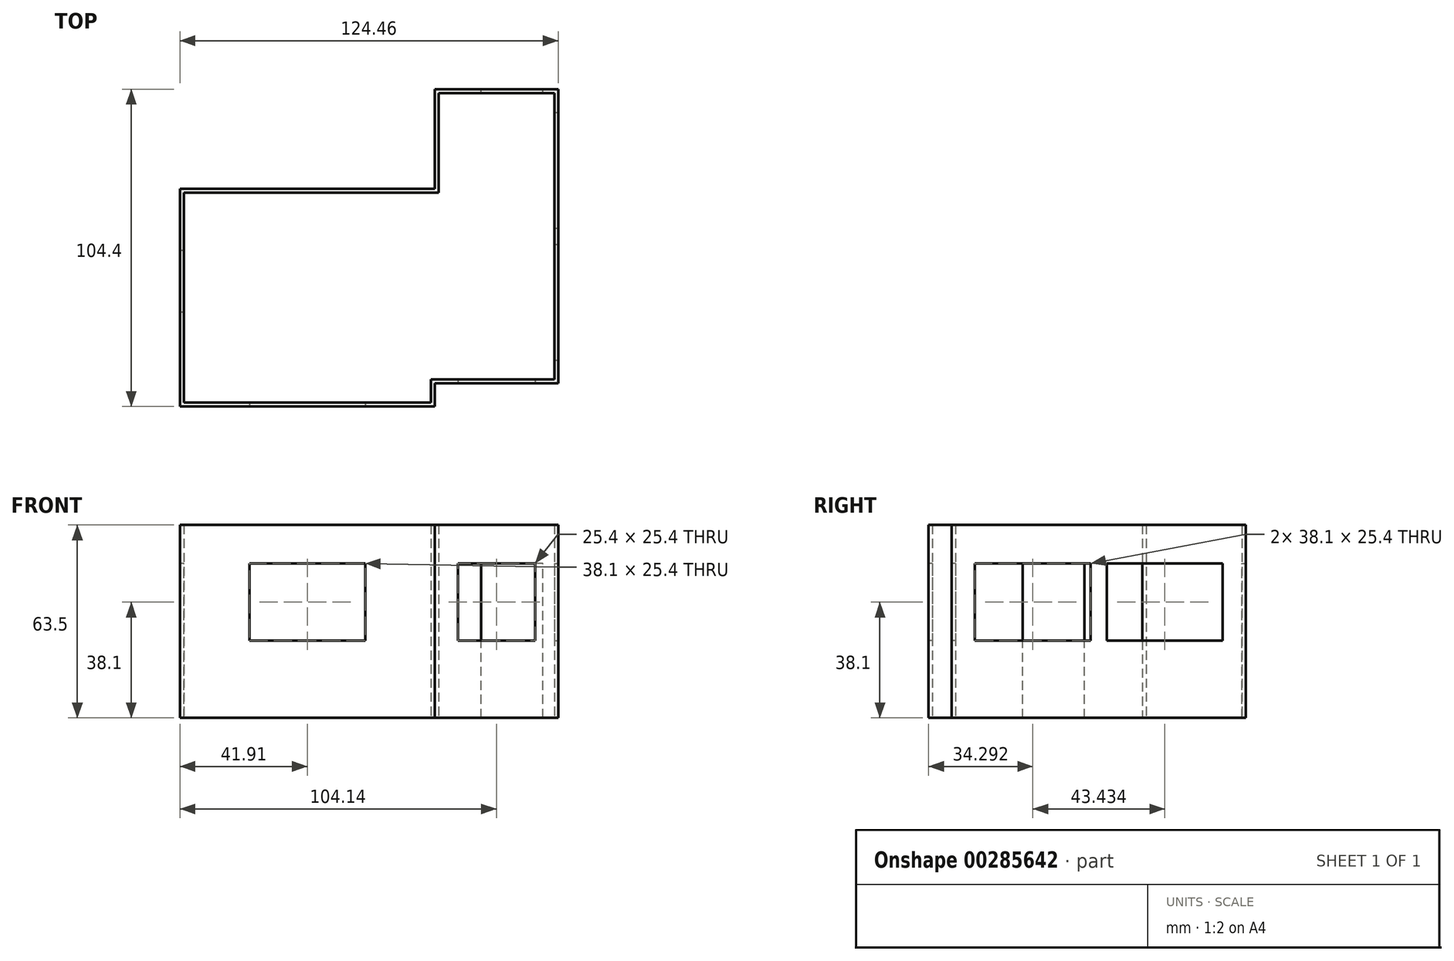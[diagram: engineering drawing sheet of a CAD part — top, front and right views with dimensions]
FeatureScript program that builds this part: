
annotation { "Feature Type Name" : "Feature", "Feature Type Description" : "" }
export const myFeature = defineFeature(function(context is Context, id is Id, definition is map)
    precondition{}
    {
        {
            var Q0;
            Q0=qCreatedBy(makeId("Top.planeOp"),FACE);
            var sketch = newSketch(context, id + "F0", { "sketchPlane" : qUnion([Q0])});
            skLineSegment(sketch, "E0.bottom", {"start": v(0, 0) * mm, "end": v(-83.82, 0) * mm});
            skLineSegment(sketch, "E0.top", {"start": v(0, -71.63) * mm, "end": v(-83.82, -71.63) * mm});
            skLineSegment(sketch, "E0.left", {"start": v(0, -64) * mm, "end": v(0, -71.63) * mm});
            skLineSegment(sketch, "E0.right", {"start": v(-83.82, 0) * mm, "end": v(-83.82, -71.63) * mm});
            skLineSegment(sketch, "E1.bottom", {"start": v(0, -64) * mm, "end": v(40.64, -64) * mm});
            skLineSegment(sketch, "E1.top", {"start": v(0, 32.77) * mm, "end": v(40.64, 32.77) * mm});
            skLineSegment(sketch, "E1.right", {"start": v(40.64, -64) * mm, "end": v(40.64, 32.77) * mm});
            skLineSegment(sketch, "E2", {"start": v(0, 32.77) * mm, "end": v(0, 0) * mm});
            skLineSegment(sketch, "E3.0", {"start": v(1.27, 31.5) * mm, "end": v(1.27, -1.27) * mm});
            skLineSegment(sketch, "E3.1", {"start": v(1.27, 31.5) * mm, "end": v(39.37, 31.5) * mm});
            skLineSegment(sketch, "E3.2", {"start": v(1.27, -1.27) * mm, "end": v(-82.55, -1.27) * mm});
            skLineSegment(sketch, "E3.3", {"start": v(39.37, -62.74) * mm, "end": v(39.37, 31.5) * mm});
            skLineSegment(sketch, "E3.4", {"start": v(-82.55, -1.27) * mm, "end": v(-82.55, -70.36) * mm});
            skLineSegment(sketch, "E3.5", {"start": v(-1.27, -70.36) * mm, "end": v(-82.55, -70.36) * mm});
            skLineSegment(sketch, "E3.6", {"start": v(-1.27, -62.74) * mm, "end": v(-1.27, -70.36) * mm});
            skLineSegment(sketch, "E3.7", {"start": v(-1.27, -62.74) * mm, "end": v(39.37, -62.74) * mm});
            skSolve(sketch);
        }
        {
            var Q0;
            Q0 = qSketchRegion(id + "F0", true);
            extrude(context, id + "F1", {"entities" : qUnion([Q0]), "depth" : 63.5 * mm});
        }
        {
            var Q0;
            Q0=makeQuery(id+"F1.opExtrude","SWEPT_FACE",FACE,{"disambiguationData":[OSD([sQuery(id+"F0.wireOp",EDGE,"E0.top")])]});
            var sketch = newSketch(context, id + "F2", { "sketchPlane" : qUnion([Q0])});
            skLineSegment(sketch, "E4.bottom", {"start": v(-60.96, 50.8) * mm, "end": v(-22.86, 50.8) * mm});
            skLineSegment(sketch, "E4.top", {"start": v(-60.96, 25.4) * mm, "end": v(-22.86, 25.4) * mm});
            skLineSegment(sketch, "E4.left", {"start": v(-60.96, 50.8) * mm, "end": v(-60.96, 25.4) * mm});
            skLineSegment(sketch, "E4.right", {"start": v(-22.86, 50.8) * mm, "end": v(-22.86, 25.4) * mm});
            skSolve(sketch);
        }
        {
            var Q0;
            Q0 = qSketchRegion(id + "F2", true);
            extrude(context, id + "F3", {"entities" : qUnion([Q0]), "operationType" : NewBodyOperationType.REMOVE, "oppositeDirection" : true, "depth" : 1.27 * mm});
        }
        {
            var Q0;
            Q0=makeQuery(id+"F1.opExtrude","SWEPT_FACE",FACE,{"disambiguationData":[OSD([sQuery(id+"F0.wireOp",EDGE,"E1.bottom")])]});
            var sketch = newSketch(context, id + "F4", { "sketchPlane" : qUnion([Q0])});
            skLineSegment(sketch, "E5.bottom", {"start": v(7.62, 50.8) * mm, "end": v(33.02, 50.8) * mm});
            skLineSegment(sketch, "E5.top", {"start": v(7.62, 25.4) * mm, "end": v(33.02, 25.4) * mm});
            skLineSegment(sketch, "E5.left", {"start": v(7.62, 50.8) * mm, "end": v(7.62, 25.4) * mm});
            skLineSegment(sketch, "E5.right", {"start": v(33.02, 50.8) * mm, "end": v(33.02, 25.4) * mm});
            skSolve(sketch);
        }
        {
            var Q0;
            Q0 = qSketchRegion(id + "F4", true);
            extrude(context, id + "F5", {"entities" : qUnion([Q0]), "operationType" : NewBodyOperationType.REMOVE, "oppositeDirection" : true, "depth" : 1.27 * mm});
        }
        {
            var Q0;
            Q0=makeQuery(id+"F1.opExtrude","SWEPT_FACE",FACE,{"disambiguationData":[OSD([sQuery(id+"F0.wireOp",EDGE,"E1.right")])]});
            var sketch = newSketch(context, id + "F6", { "sketchPlane" : qUnion([Q0])});
            skLineSegment(sketch, "E6.bottom", {"start": v(-56.39, 50.8) * mm, "end": v(-18.29, 50.8) * mm});
            skLineSegment(sketch, "E6.top", {"start": v(-56.39, 25.4) * mm, "end": v(-18.29, 25.4) * mm});
            skLineSegment(sketch, "E6.left", {"start": v(-56.39, 50.8) * mm, "end": v(-56.39, 25.4) * mm});
            skLineSegment(sketch, "E6.right", {"start": v(-18.29, 50.8) * mm, "end": v(-18.29, 25.4) * mm});
            skLineSegment(sketch, "E7.bottom", {"start": v(-12.95, 50.8) * mm, "end": v(25.15, 50.8) * mm});
            skLineSegment(sketch, "E7.top", {"start": v(-12.95, 25.4) * mm, "end": v(25.15, 25.4) * mm});
            skLineSegment(sketch, "E7.left", {"start": v(-12.95, 50.8) * mm, "end": v(-12.95, 25.4) * mm});
            skLineSegment(sketch, "E7.right", {"start": v(25.15, 50.8) * mm, "end": v(25.15, 25.4) * mm});
            skSolve(sketch);
        }
        {
            var Q0;
            Q0 = qSketchRegion(id + "F6", true);
            extrude(context, id + "F7", {"entities" : qUnion([Q0]), "operationType" : NewBodyOperationType.REMOVE, "oppositeDirection" : true, "depth" : 1.27 * mm});
        }
        {
            var Q0;
            Q0=makeQuery(id+"F1.opExtrude","SWEPT_FACE",FACE,{"disambiguationData":[OSD([sQuery(id+"F0.wireOp",EDGE,"E1.top")])]});
            var sketch = newSketch(context, id + "F8", { "sketchPlane" : qUnion([Q0])});
            skLineSegment(sketch, "E8.bottom", {"start": v(-35.56, 0) * mm, "end": v(-15.24, 0) * mm});
            skLineSegment(sketch, "E8.top", {"start": v(-35.56, 50.8) * mm, "end": v(-15.24, 50.8) * mm});
            skLineSegment(sketch, "E8.left", {"start": v(-35.56, 0) * mm, "end": v(-35.56, 50.8) * mm});
            skLineSegment(sketch, "E8.right", {"start": v(-15.24, 0) * mm, "end": v(-15.24, 50.8) * mm});
            skSolve(sketch);
        }
        {
            var Q0;
            Q0 = qSketchRegion(id + "F8", true);
            extrude(context, id + "F9", {"entities" : qUnion([Q0]), "operationType" : NewBodyOperationType.REMOVE, "oppositeDirection" : true, "depth" : 1.27 * mm});
        }
        {
            var Q0;
            Q0=makeQuery(id+"F1.opExtrude","SWEPT_FACE",FACE,{"disambiguationData":[OSD([sQuery(id+"F0.wireOp",EDGE,"E0.right")])]});
            var sketch = newSketch(context, id + "F10", { "sketchPlane" : qUnion([Q0])});
            skLineSegment(sketch, "E9.bottom", {"start": v(20.32, 0) * mm, "end": v(40.64, 0) * mm});
            skLineSegment(sketch, "E9.top", {"start": v(20.32, 50.8) * mm, "end": v(40.64, 50.8) * mm});
            skLineSegment(sketch, "E9.left", {"start": v(20.32, 0) * mm, "end": v(20.32, 50.8) * mm});
            skLineSegment(sketch, "E9.right", {"start": v(40.64, 0) * mm, "end": v(40.64, 50.8) * mm});
            skSolve(sketch);
        }
        {
            var Q0;
            Q0 = qSketchRegion(id + "F10", true);
            extrude(context, id + "F11", {"entities" : qUnion([Q0]), "operationType" : NewBodyOperationType.REMOVE, "oppositeDirection" : true, "depth" : 1.27 * mm});
        }
    });
